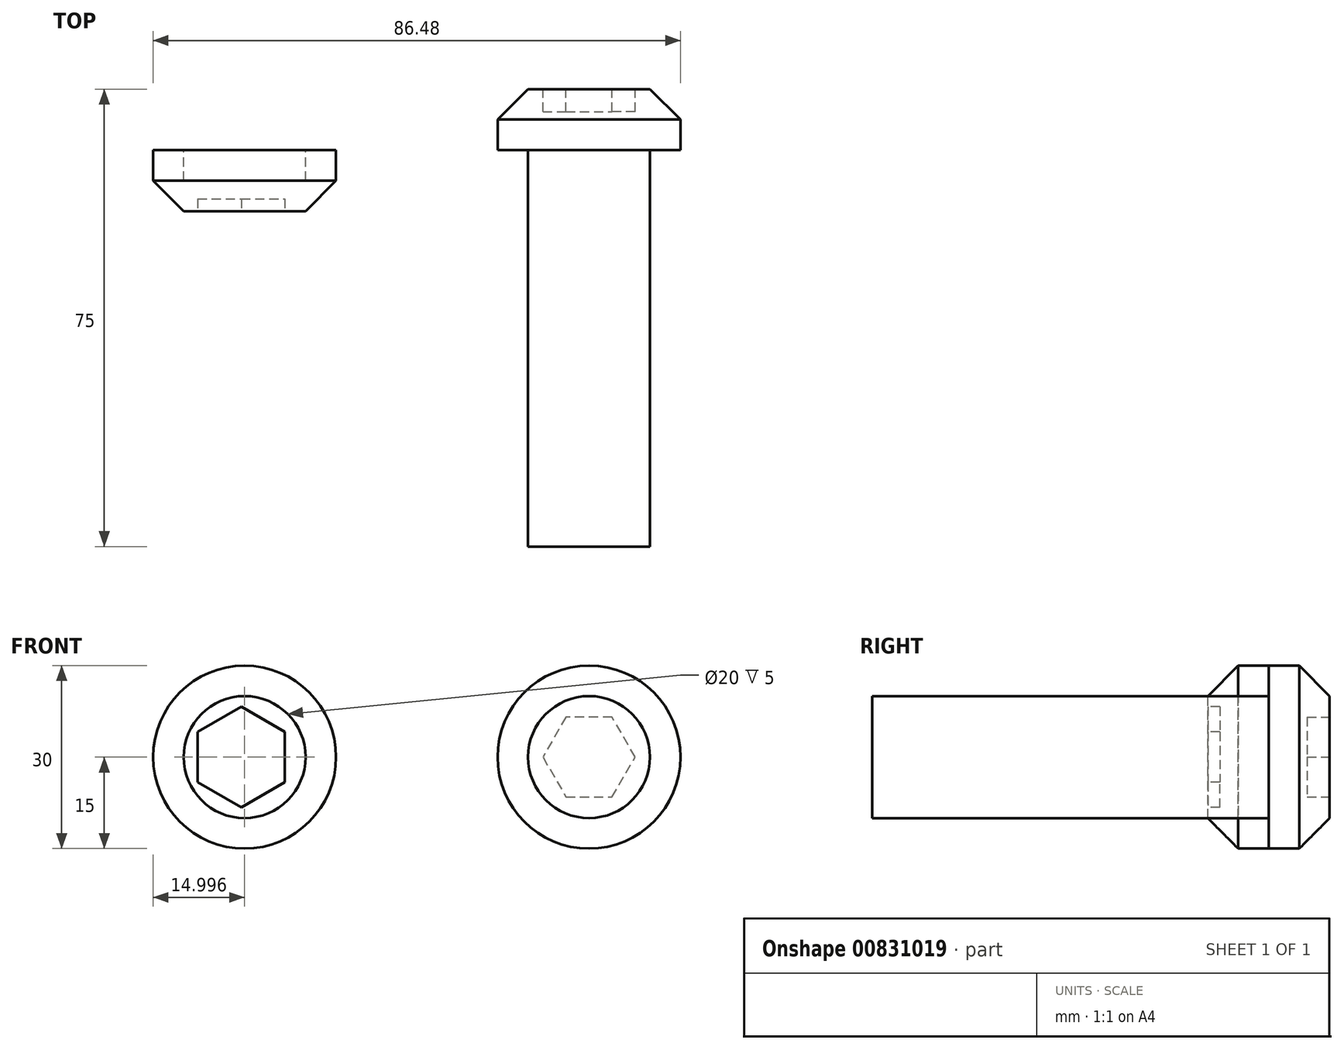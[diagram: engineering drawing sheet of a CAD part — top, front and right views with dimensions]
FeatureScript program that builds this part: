
annotation { "Feature Type Name" : "Feature", "Feature Type Description" : "" }
export const myFeature = defineFeature(function(context is Context, id is Id, definition is map)
    precondition{}
    {
        {
            var Q0;
            Q0=qCreatedBy(makeId("Front.planeOp"),FACE);
            var sketch = newSketch(context, id + "F0", { "sketchPlane" : qUnion([Q0])});
            skCircle(sketch, "E0", {"center": v(0, 0) * mm, "radius": 10 * mm});
            skCircle(sketch, "E1", {"center": v(0, 0) * mm, "radius": 15 * mm});
            skCircle(sketch, "E2", {"center": v(-56.48, 0) * mm, "radius": 10 * mm});
            skCircle(sketch, "E3", {"center": v(-56.48, 0) * mm, "radius": 15 * mm});
            skSolve(sketch);
        }
        {
            var Q0;
            Q0=makeQuery(id+"F0.imprint","IMPRINT",FACE,{"disambiguationData":[TD([[makeQuery(id+"F0.imprint","IMPRINT",EDGE,{"derivedFrom":sQuery(id+"F0.wireOp",EDGE,"E0")}),1.0]])]});
            extrude(context, id + "F1", {"entities" : qUnion([Q0]), "depth" : 65 * mm, "offsetDistance" : 25 * mm});
        }
        {
            var Q0;
            Q0=makeQuery(id+"F0.imprint","IMPRINT",FACE,{"disambiguationData":[TD([[makeQuery(id+"F0.imprint","IMPRINT",EDGE,{"derivedFrom":sQuery(id+"F0.wireOp",EDGE,"E0")}),-1.0]])]});
            var Q1;
            Q1=makeQuery(id+"F0.imprint","IMPRINT",FACE,{"disambiguationData":[TD([[makeQuery(id+"F0.imprint","IMPRINT",EDGE,{"derivedFrom":sQuery(id+"F0.wireOp",EDGE,"E0")}),1.0]])]});
            extrude(context, id + "F2", {"entities" : qUnion([Q0, Q1]), "operationType" : NewBodyOperationType.ADD, "oppositeDirection" : true, "depth" : 10 * mm, "offsetDistance" : 25 * mm});
        }
        {
            var Q0;
            Q0=makeQuery(id+"F0.imprint","IMPRINT",FACE,{"disambiguationData":[TD([[makeQuery(id+"F0.imprint","IMPRINT",EDGE,{"derivedFrom":sQuery(id+"F0.wireOp",EDGE,"E2")}),1.0]])]});
            var Q1;
            Q1=makeQuery(id+"F0.imprint","IMPRINT",FACE,{"disambiguationData":[TD([[makeQuery(id+"F0.imprint","IMPRINT",EDGE,{"derivedFrom":sQuery(id+"F0.wireOp",EDGE,"E2")}),-1.0]])]});
            extrude(context, id + "F3", {"entities" : qUnion([Q0, Q1]), "depth" : 10 * mm, "offsetDistance" : 25 * mm});
        }
        {
            var Q0;
            Q0=makeQuery(id+"F0.imprint","IMPRINT",FACE,{"disambiguationData":[TD([[makeQuery(id+"F0.imprint","IMPRINT",EDGE,{"derivedFrom":sQuery(id+"F0.wireOp",EDGE,"E2")}),1.0]])]});
            extrude(context, id + "F4", {"entities" : qUnion([Q0]), "operationType" : NewBodyOperationType.REMOVE, "depth" : 5 * mm, "offsetDistance" : 25 * mm});
        }
        {
            var Q0;
            Q0=makeQuery(id+"F2.opExtrude","CAP_EDGE",EDGE,{"disambiguationData":[OSD([sQuery(id+"F0.wireOp",EDGE,"E1")])],"isStart":false});
            var Q1;
            Q1=makeQuery(id+"F3.opExtrude","CAP_EDGE",EDGE,{"disambiguationData":[OSD([sQuery(id+"F0.wireOp",EDGE,"E3")])],"isStart":false});
            chamfer(context, id + "F5", {"entities" : qUnion([Q0, Q1]), "width" : 5 * mm, "tangentPropagation" : true});
        }
        {
            var Q0;
            Q0=makeQuery(id+"F2.opExtrude","CAP_FACE",FACE,{"disambiguationData":[OSD([sQuery(id+"F0.wireOp",EDGE,"E1")])],"isStart":false});
            var sketch = newSketch(context, id + "F6", { "sketchPlane" : qUnion([Q0])});
            skCircle(sketch, "E4.cCircle", {"center": v(0, 0) * mm, "radius": 6.55 * mm, "construction": true});
            skLineSegment(sketch, "E4.0", {"start": v(3.78, -6.55) * mm, "end": v(-3.78, -6.55) * mm});
            skLineSegment(sketch, "E4.1", {"start": v(-3.78, -6.55) * mm, "end": v(-7.56, 0) * mm});
            skLineSegment(sketch, "E4.2", {"start": v(-7.56, 0) * mm, "end": v(-3.78, 6.55) * mm});
            skLineSegment(sketch, "E4.3", {"start": v(-3.78, 6.55) * mm, "end": v(3.78, 6.55) * mm});
            skLineSegment(sketch, "E4.4", {"start": v(3.78, 6.55) * mm, "end": v(7.56, 0) * mm});
            skLineSegment(sketch, "E4.5", {"start": v(7.56, 0) * mm, "end": v(3.78, -6.55) * mm});
            skPoint(sketch, "E4.0.midPoint", {"position": v(0, -6.55) * mm});
            skSolve(sketch);
        }
        {
            var Q0;
            Q0 = qSketchRegion(id + "F6", true);
            extrude(context, id + "F7", {"entities" : qUnion([Q0]), "operationType" : NewBodyOperationType.REMOVE, "oppositeDirection" : true, "depth" : 3.7 * mm, "offsetDistance" : 25 * mm});
        }
        {
            var Q0;
            Q0=qCreatedBy(makeId("Front.planeOp"),FACE);
            cPlane(context, id + "F8", {"entities" : qUnion([Q0]), "cplaneType" : CPlaneType.OFFSET, "offset" : 10 * mm, "width" : 150 * mm, "height" : 150 * mm});
        }
        {
            var Q0;
            Q0=qCreatedBy(id+"F8.planeOp",FACE);
            var sketch = newSketch(context, id + "F9", { "sketchPlane" : qUnion([Q0])});
            skCircle(sketch, "E5.cCircle", {"center": v(-57.03, 0) * mm, "radius": 7.15 * mm, "construction": true});
            skLineSegment(sketch, "E5.0", {"start": v(-49.88, 4.13) * mm, "end": v(-49.88, -4.13) * mm});
            skLineSegment(sketch, "E5.1", {"start": v(-49.88, -4.13) * mm, "end": v(-57.03, -8.25) * mm});
            skLineSegment(sketch, "E5.2", {"start": v(-57.03, -8.25) * mm, "end": v(-64.18, -4.13) * mm});
            skLineSegment(sketch, "E5.3", {"start": v(-64.18, -4.13) * mm, "end": v(-64.18, 4.13) * mm});
            skLineSegment(sketch, "E5.4", {"start": v(-64.18, 4.13) * mm, "end": v(-57.03, 8.25) * mm});
            skLineSegment(sketch, "E5.5", {"start": v(-57.03, 8.25) * mm, "end": v(-49.88, 4.13) * mm});
            skPoint(sketch, "E5.0.midPoint", {"position": v(-49.88, 0) * mm});
            skSolve(sketch);
        }
        {
            var Q0;
            Q0 = qSketchRegion(id + "F9", true);
            extrude(context, id + "F10", {"entities" : qUnion([Q0]), "operationType" : NewBodyOperationType.REMOVE, "oppositeDirection" : true, "depth" : 2 * mm, "offsetDistance" : 25 * mm});
        }
    });
